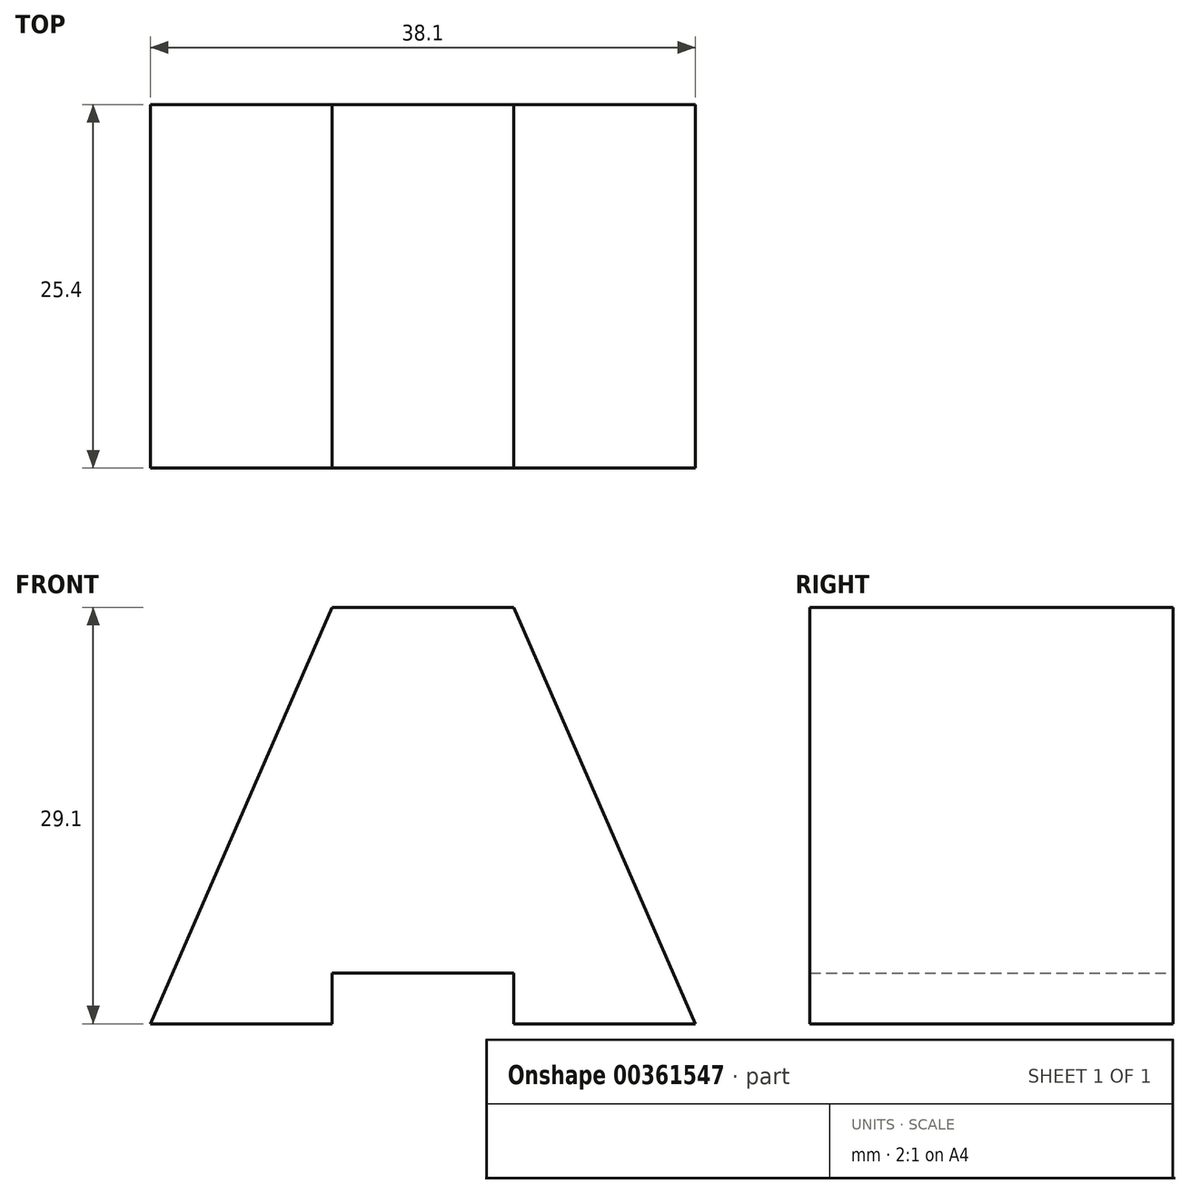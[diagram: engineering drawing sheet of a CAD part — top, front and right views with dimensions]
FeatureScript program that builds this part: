
annotation { "Feature Type Name" : "Feature", "Feature Type Description" : "" }
export const myFeature = defineFeature(function(context is Context, id is Id, definition is map)
    precondition{}
    {
        {
            var Q0;
            Q0=qCreatedBy(makeId("Front.planeOp"),FACE);
            var sketch = newSketch(context, id + "F0", { "sketchPlane" : qUnion([Q0])});
            skLineSegment(sketch, "E0", {"start": v(-23.04, 0) * mm, "end": v(-10.34, 29.1) * mm});
            skLineSegment(sketch, "E1", {"start": v(-10.34, 29.1) * mm, "end": v(2.36, 29.1) * mm});
            skLineSegment(sketch, "E2", {"start": v(2.36, 29.1) * mm, "end": v(15.06, 0) * mm});
            skLineSegment(sketch, "E3", {"start": v(-23.04, 0) * mm, "end": v(-10.34, 0) * mm});
            skLineSegment(sketch, "E4", {"start": v(-10.34, 0) * mm, "end": v(-10.34, 3.54) * mm});
            skLineSegment(sketch, "E5", {"start": v(-10.34, 3.54) * mm, "end": v(2.36, 3.54) * mm});
            skLineSegment(sketch, "E6", {"start": v(2.36, 3.54) * mm, "end": v(2.36, 0) * mm});
            skLineSegment(sketch, "E7", {"start": v(2.36, 0) * mm, "end": v(15.06, 0) * mm});
            skSolve(sketch);
        }
        {
            var Q0;
            Q0=makeQuery(id+"F0.imprint","IMPRINT",FACE,{"disambiguationData":[TD([[makeQuery(id+"F0.imprint","IMPRINT",EDGE,{"derivedFrom":sQuery(id+"F0.wireOp",EDGE,"E0")}),-1.0]])]});
            extrude(context, id + "F1", {"entities" : qUnion([Q0]), "depth" : 25.4 * mm});
        }
    });
